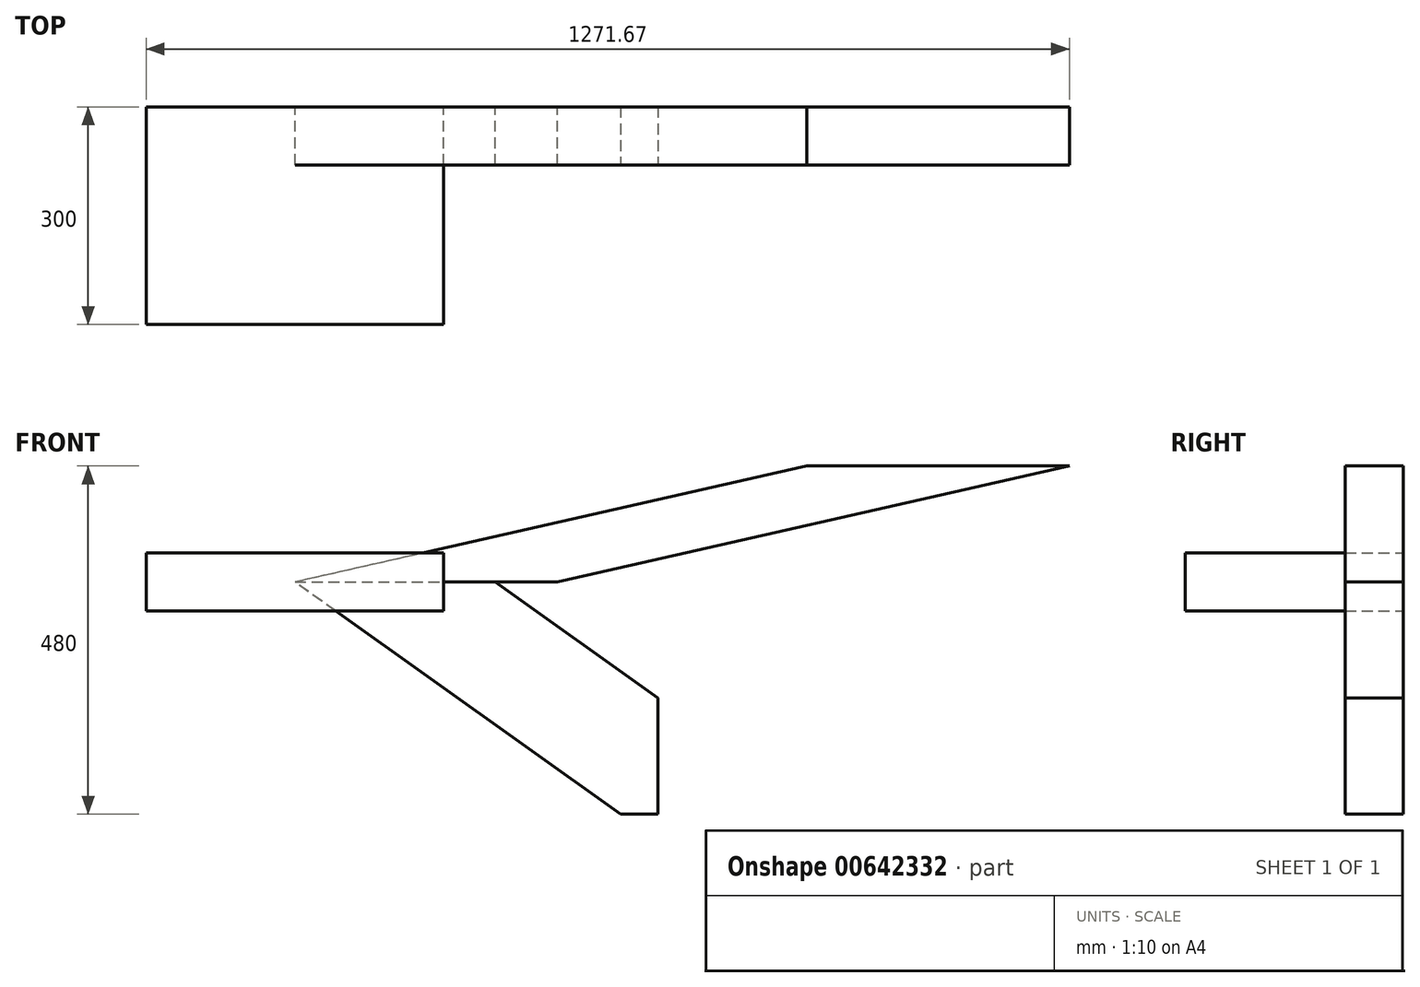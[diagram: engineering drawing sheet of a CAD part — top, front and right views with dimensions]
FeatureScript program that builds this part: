
annotation { "Feature Type Name" : "Feature", "Feature Type Description" : "" }
export const myFeature = defineFeature(function(context is Context, id is Id, definition is map)
    precondition{}
    {
        {
            var Q0;
            Q0=qCreatedBy(makeId("Front.planeOp"),FACE);
            var sketch = newSketch(context, id + "F0", { "sketchPlane" : qUnion([Q0])});
            skLineSegment(sketch, "E0", {"start": v(0, 0) * mm, "end": v(275.6, 0) * mm});
            skLineSegment(sketch, "E1", {"start": v(275.6, 0) * mm, "end": v(500, -160) * mm});
            skLineSegment(sketch, "E2", {"start": v(500, -160) * mm, "end": v(500, -356.5) * mm});
            skLineSegment(sketch, "E3", {"start": v(500, -356.5) * mm, "end": v(0, 0) * mm});
            skSolve(sketch);
        }
        {
            var Q0;
            Q0=makeQuery(id+"F0.imprint","IMPRINT",FACE,{"disambiguationData":[TD([[makeQuery(id+"F0.imprint","IMPRINT",EDGE,{"derivedFrom":sQuery(id+"F0.wireOp",EDGE,"E0")}),-1.0]])]});
            extrude(context, id + "F1", {"entities" : qUnion([Q0]), "depth" : 80 * mm, "offsetDistance" : 25 * mm});
        }
        {
            var Q0;
            Q0=makeQuery(id+"F1.opExtrude","CAP_FACE",FACE,{"disambiguationData":[OSD([sQuery(id+"F0.wireOp",EDGE,"E0"),sQuery(id+"F0.wireOp",EDGE,"E1"),sQuery(id+"F0.wireOp",EDGE,"E2"),sQuery(id+"F0.wireOp",EDGE,"E3")])],"isStart":false});
            var sketch = newSketch(context, id + "F2", { "sketchPlane" : qUnion([Q0])});
            skLineSegment(sketch, "E4", {"start": v(500, -320) * mm, "end": v(448.8, -320) * mm});
            skSolve(sketch);
        }
        {
            var Q0;
            {var subQ0=sQuery(id+"F2.wireOp",EDGE,"E4");Q0=makeQuery(id+"F2.imprint","IMPRINT",FACE,{"disambiguationData":[TD([[makeQuery(id+"F2.imprint","IMPRINT",EDGE,{"derivedFrom":subQ0}),1.0]])]});}
            extrude(context, id + "F3", {"entities" : qUnion([Q0]), "operationType" : NewBodyOperationType.REMOVE, "endBound" : BoundingType.THROUGH_ALL, "oppositeDirection" : true, "depth" : 25 * mm, "offsetDistance" : 25 * mm});
        }
        {
            var Q0;
            Q0=qCreatedBy(makeId("Front.planeOp"),FACE);
            var sketch = newSketch(context, id + "F4", { "sketchPlane" : qUnion([Q0])});
            skLineSegment(sketch, "E5", {"start": v(0, 0) * mm, "end": v(361.53, 0) * mm});
            skLineSegment(sketch, "E6", {"start": v(361.53, 0) * mm, "end": v(1066.67, 160) * mm});
            skLineSegment(sketch, "E7", {"start": v(1066.67, 160) * mm, "end": v(705.14, 160) * mm});
            skLineSegment(sketch, "E8", {"start": v(705.14, 160) * mm, "end": v(0, 0) * mm});
            skSolve(sketch);
        }
        {
            var Q0;
            Q0=makeQuery(id+"F4.imprint","IMPRINT",FACE,{"disambiguationData":[TD([[makeQuery(id+"F4.imprint","IMPRINT",EDGE,{"derivedFrom":sQuery(id+"F4.wireOp",EDGE,"E5")}),1.0]])]});
            extrude(context, id + "F5", {"entities" : qUnion([Q0]), "depth" : 80 * mm, "offsetDistance" : 25 * mm});
        }
        {
            var Q0;
            Q0=qCreatedBy(makeId("Front.planeOp"),FACE);
            var sketch = newSketch(context, id + "F6", { "sketchPlane" : qUnion([Q0])});
            skLineSegment(sketch, "E9.bottom", {"start": v(205, 40) * mm, "end": v(-205, 40) * mm});
            skLineSegment(sketch, "E9.top", {"start": v(205, -40) * mm, "end": v(-205, -40) * mm});
            skLineSegment(sketch, "E9.left", {"start": v(205, 40) * mm, "end": v(205, -40) * mm});
            skLineSegment(sketch, "E9.right", {"start": v(-205, 40) * mm, "end": v(-205, -40) * mm});
            skPoint(sketch, "E9.middle", {"position": v(0, 0) * mm});
            skSolve(sketch);
        }
        {
            var Q0;
            Q0=makeQuery(id+"F6.imprint","IMPRINT",FACE,{"disambiguationData":[TD([[makeQuery(id+"F6.imprint","IMPRINT",EDGE,{"derivedFrom":sQuery(id+"F6.wireOp",EDGE,"E9.bottom")}),1.0]])]});
            extrude(context, id + "F7", {"entities" : qUnion([Q0]), "depth" : 300 * mm, "offsetDistance" : 25 * mm});
        }
    });
